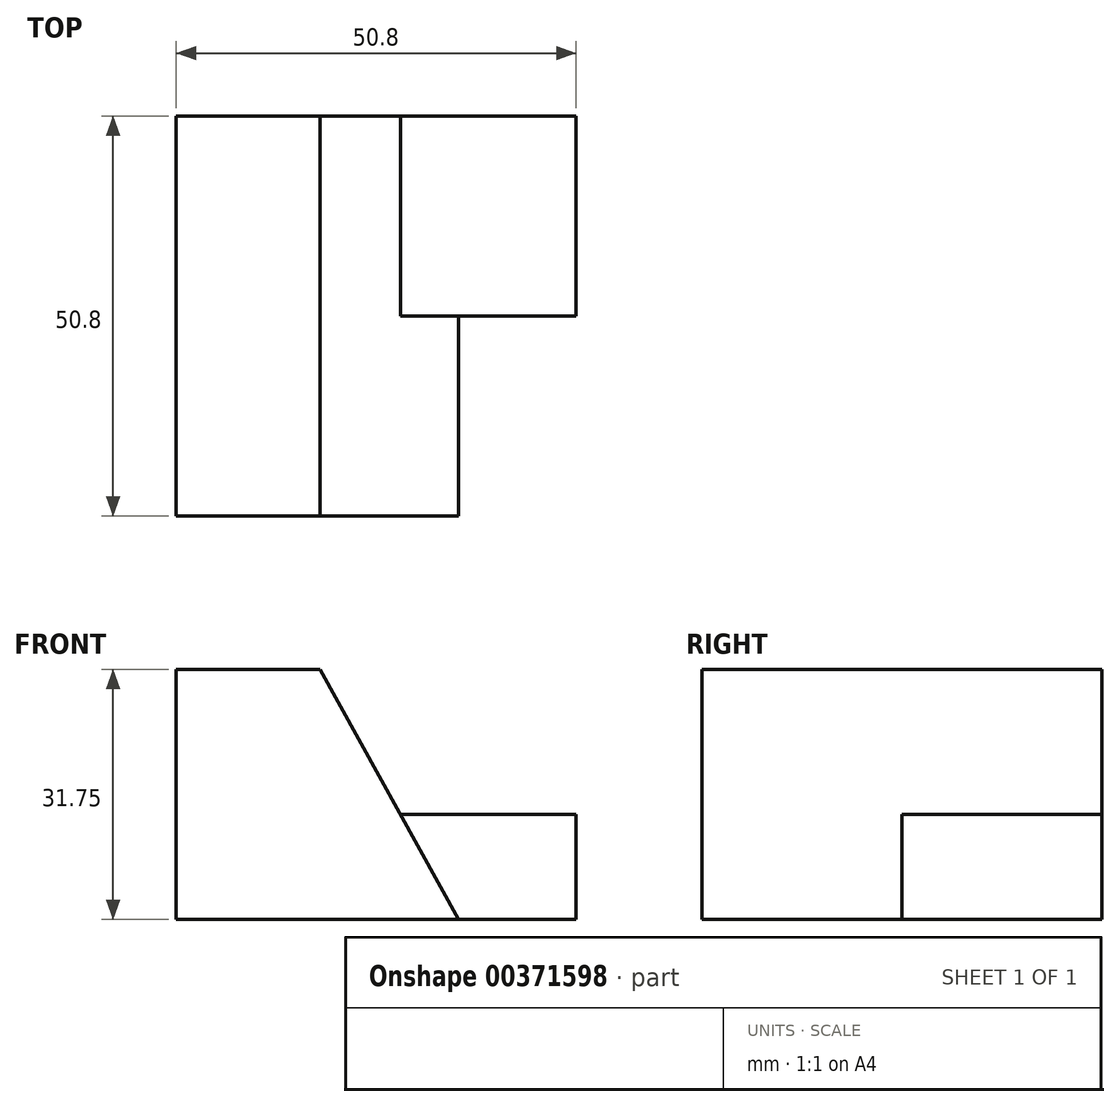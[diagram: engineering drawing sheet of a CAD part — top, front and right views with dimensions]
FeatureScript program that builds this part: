
annotation { "Feature Type Name" : "Feature", "Feature Type Description" : "" }
export const myFeature = defineFeature(function(context is Context, id is Id, definition is map)
    precondition{}
    {
        {
            var Q0;
            Q0=qCreatedBy(makeId("Front.planeOp"),FACE);
            var sketch = newSketch(context, id + "F0", { "sketchPlane" : qUnion([Q0])});
            skLineSegment(sketch, "E0", {"start": v(0, 0) * mm, "end": v(0, 31.75) * mm});
            skLineSegment(sketch, "E1", {"start": v(0, 31.75) * mm, "end": v(50.8, 31.75) * mm});
            skLineSegment(sketch, "E2", {"start": v(50.8, 31.75) * mm, "end": v(50.8, 0) * mm});
            skLineSegment(sketch, "E3", {"start": v(50.8, 0) * mm, "end": v(0, 0) * mm});
            skSolve(sketch);
        }
        {
            var Q0;
            Q0 = qSketchRegion(id + "F0", true);
            extrude(context, id + "F1", {"entities" : qUnion([Q0]), "depth" : 50.8 * mm});
        }
        {
            var Q0;
            Q0=makeQuery(id+"F1.opExtrude","CAP_FACE",FACE,{"disambiguationData":[OSD([sQuery(id+"F0.wireOp",EDGE,"E0"),sQuery(id+"F0.wireOp",EDGE,"E1"),sQuery(id+"F0.wireOp",EDGE,"E2"),sQuery(id+"F0.wireOp",EDGE,"E3")])],"isStart":false});
            var sketch = newSketch(context, id + "F2", { "sketchPlane" : qUnion([Q0])});
            skLineSegment(sketch, "E4", {"start": v(0, 31.75) * mm, "end": v(18.3, 31.75) * mm});
            skLineSegment(sketch, "E5", {"start": v(18.3, 31.75) * mm, "end": v(35.9, 0) * mm});
            skSolve(sketch);
        }
        {
            var Q0;
            {var subQ0=sQuery(id+"F2.wireOp",EDGE,"E5");Q0=makeQuery(id+"F2.imprint","IMPRINT",FACE,{"disambiguationData":[TD([[makeQuery(id+"F2.imprint","IMPRINT",EDGE,{"derivedFrom":subQ0}),1.0]])]});}
            extrude(context, id + "F3", {"entities" : qUnion([Q0]), "operationType" : NewBodyOperationType.REMOVE, "oppositeDirection" : true, "depth" : 25.4 * mm});
        }
        {
            var Q0;
            Q0=makeQuery(id+"F3.boolean.opBoolean","COPY",FACE,{"derivedFrom":makeQuery(id+"F3.opExtrude","CAP_FACE",FACE,{"disambiguationData":[OSD([sQuery(id+"F0.wireOp",EDGE,"E1"),sQuery(id+"F0.wireOp",EDGE,"E2"),sQuery(id+"F0.wireOp",EDGE,"E3"),sQuery(id+"F2.wireOp",EDGE,"E5")])],"isStart":false})});
            var sketch = newSketch(context, id + "F4", { "sketchPlane" : qUnion([Q0])});
            skLineSegment(sketch, "E6", {"start": v(35.9, 0) * mm, "end": v(28.5, 13.35) * mm});
            skLineSegment(sketch, "E7", {"start": v(28.5, 13.35) * mm, "end": v(50.8, 13.35) * mm});
            skLineSegment(sketch, "E8", {"start": v(50.8, 13.35) * mm, "end": v(50.8, 0) * mm});
            skLineSegment(sketch, "E9", {"start": v(50.8, 0) * mm, "end": v(35.9, 0) * mm});
            skSolve(sketch);
        }
        {
            var Q0;
            {var subQ0=sQuery(id+"F4.wireOp",EDGE,"E7");Q0=makeQuery(id+"F4.imprint","IMPRINT",FACE,{"disambiguationData":[TD([[makeQuery(id+"F4.imprint","IMPRINT",EDGE,{"derivedFrom":subQ0}),1.0]])]});}
            extrude(context, id + "F5", {"entities" : qUnion([Q0]), "operationType" : NewBodyOperationType.REMOVE, "oppositeDirection" : true, "depth" : 25.4 * mm});
        }
    });
